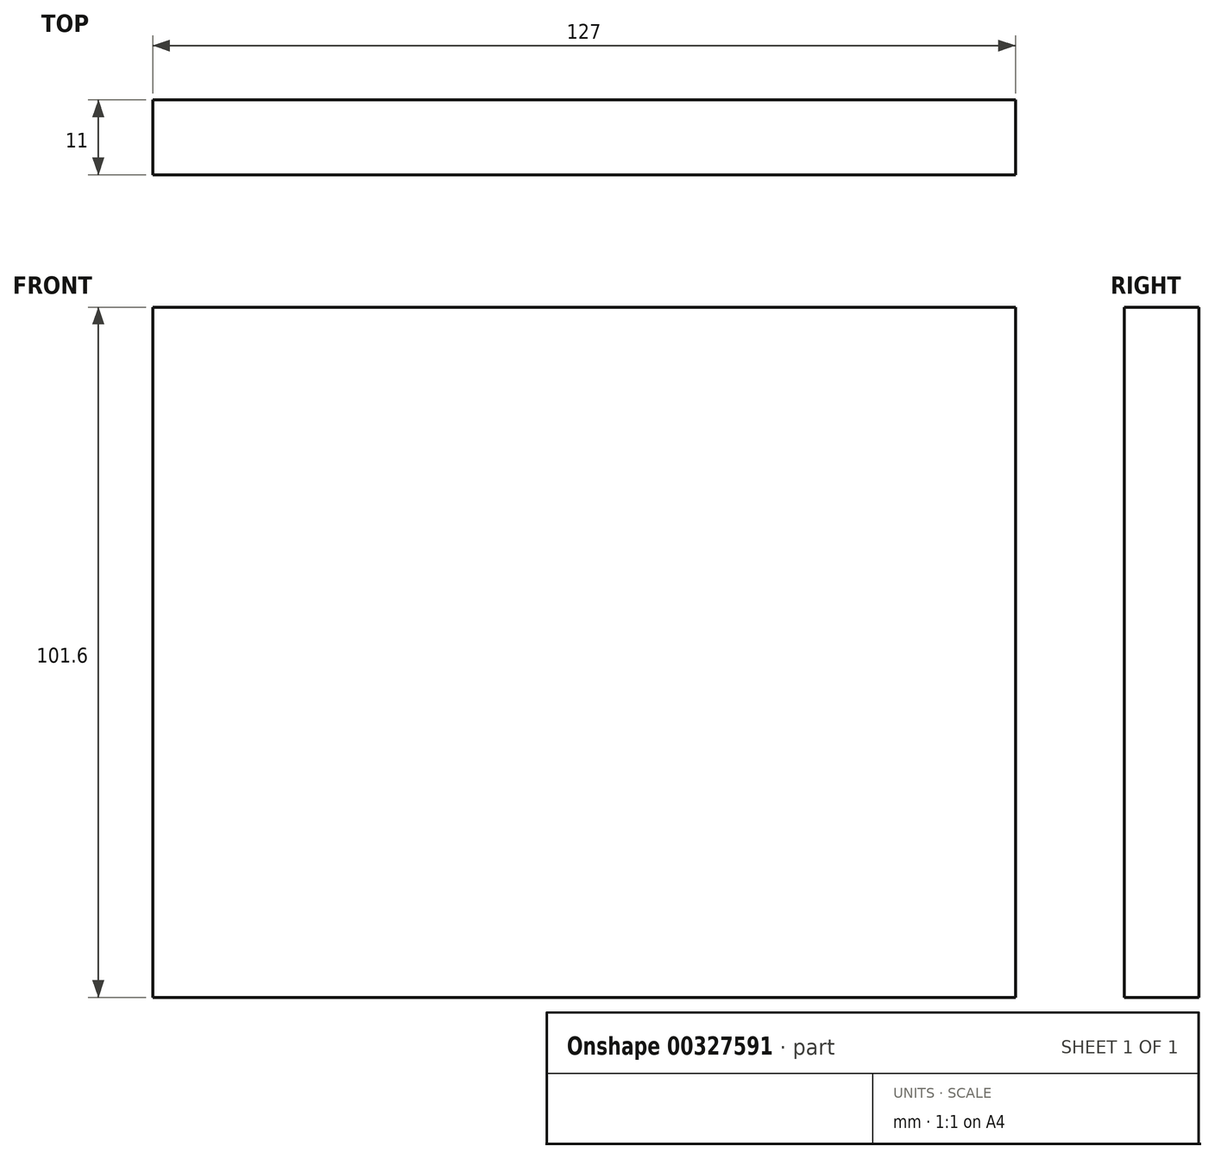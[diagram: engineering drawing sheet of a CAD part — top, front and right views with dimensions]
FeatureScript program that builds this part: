
annotation { "Feature Type Name" : "Feature", "Feature Type Description" : "" }
export const myFeature = defineFeature(function(context is Context, id is Id, definition is map)
    precondition{}
    {
        {
            var Q0;
            Q0=qCreatedBy(makeId("Front.planeOp"),FACE);
            var sketch = newSketch(context, id + "F0", { "sketchPlane" : qUnion([Q0])});
            skLineSegment(sketch, "E0.bottom", {"start": v(63.5, -50.8) * mm, "end": v(-63.5, -50.8) * mm});
            skLineSegment(sketch, "E0.top", {"start": v(63.5, 50.8) * mm, "end": v(-63.5, 50.8) * mm});
            skLineSegment(sketch, "E0.left", {"start": v(63.5, -50.8) * mm, "end": v(63.5, 50.8) * mm});
            skLineSegment(sketch, "E0.right", {"start": v(-63.5, -50.8) * mm, "end": v(-63.5, 50.8) * mm});
            skPoint(sketch, "E0.middle", {"position": v(0, 0) * mm});
            skSolve(sketch);
        }
        {
            var Q0;
            Q0=makeQuery(id+"F0.imprint","IMPRINT",FACE,{"disambiguationData":[TD([[makeQuery(id+"F0.imprint","IMPRINT",EDGE,{"derivedFrom":sQuery(id+"F0.wireOp",EDGE,"E0.bottom")}),-1.0]])]});
            extrude(context, id + "F1", {"entities" : qUnion([Q0]), "depth" : 7 * mm, "hasSecondDirection" : true, "secondDirectionOppositeDirection" : true, "secondDirectionDepth" : 4 * mm});
        }
        {
            var Q0;
            Q0=makeQuery(id+"F1.opExtrude","CAP_FACE",FACE,{"disambiguationData":[OSD([sQuery(id+"F0.wireOp",EDGE,"E0.bottom"),sQuery(id+"F0.wireOp",EDGE,"E0.top"),sQuery(id+"F0.wireOp",EDGE,"E0.left"),sQuery(id+"F0.wireOp",EDGE,"E0.right")])],"isStart":false});
            var sketch = newSketch(context, id + "F2", { "sketchPlane" : qUnion([Q0])});
            skSolve(sketch);
        }
    });
